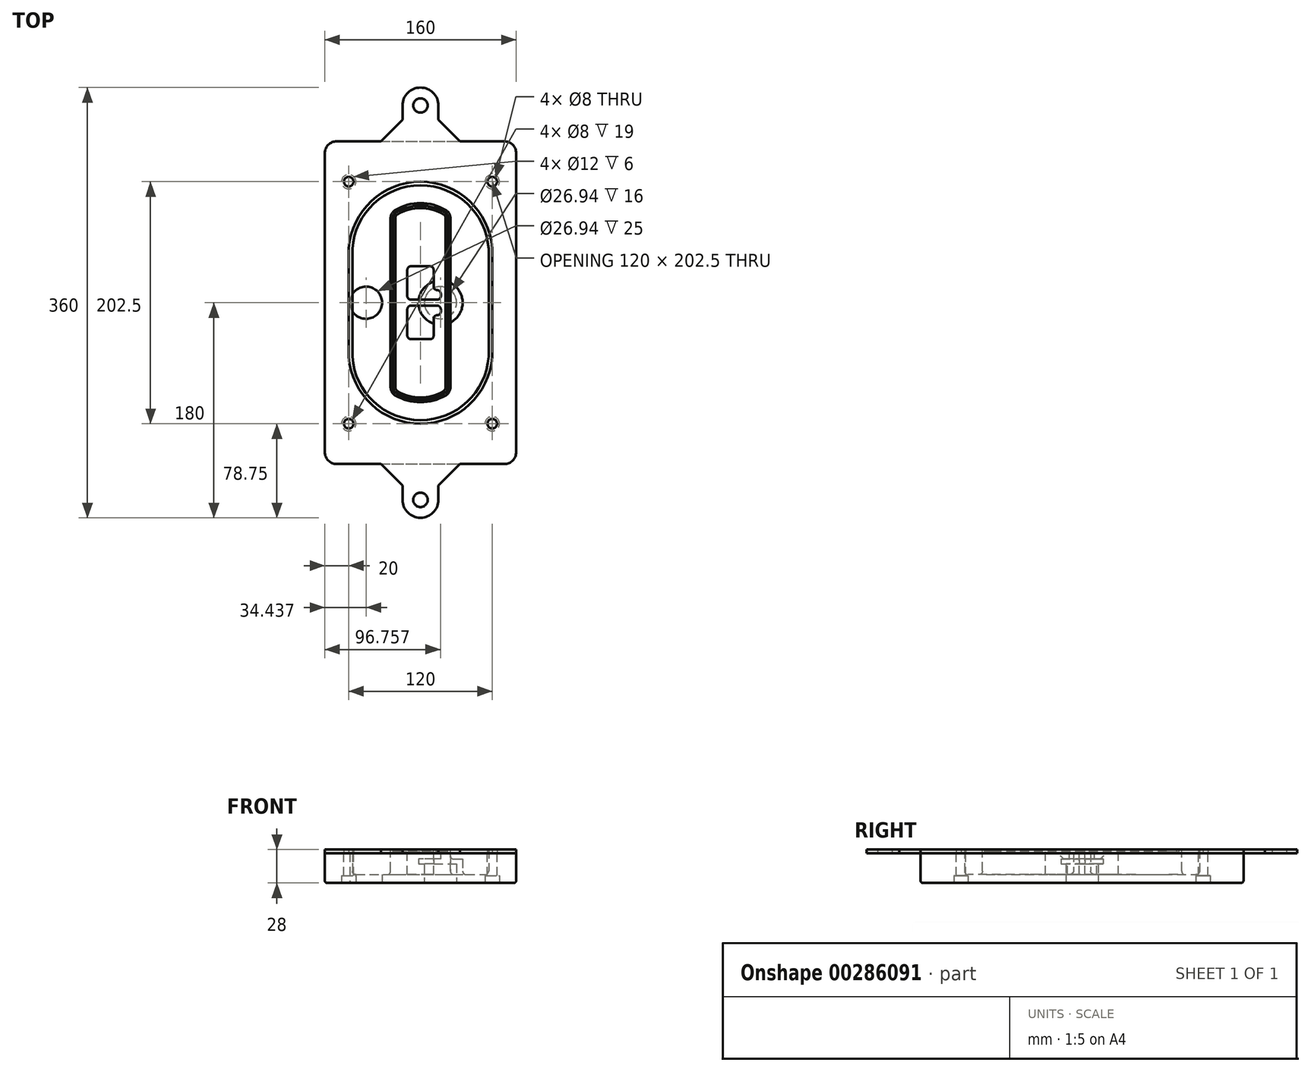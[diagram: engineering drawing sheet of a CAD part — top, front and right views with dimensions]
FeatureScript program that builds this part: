
annotation { "Feature Type Name" : "Feature", "Feature Type Description" : "" }
export const myFeature = defineFeature(function(context is Context, id is Id, definition is map)
    precondition{}
    {
        {
            var Q0;
            Q0=qCreatedBy(makeId("Top.planeOp"),FACE);
            var sketch = newSketch(context, id + "F0", { "sketchPlane" : qUnion([Q0])});
            skPoint(sketch, "E0.rect.middle", {"position": v(0, 0) * mm});
            skLineSegment(sketch, "E1.bottom", {"start": v(-70, -135) * mm, "end": v(70, -135) * mm});
            skLineSegment(sketch, "E1.top", {"start": v(-70, 135) * mm, "end": v(70, 135) * mm});
            skLineSegment(sketch, "E1.left", {"start": v(-80, -125) * mm, "end": v(-80, 125) * mm});
            skLineSegment(sketch, "E1.right", {"start": v(80, -125) * mm, "end": v(80, 125) * mm});
            skLineSegment(sketch, "E2", {"start": v(-80, 135) * mm, "end": v(80, -135) * mm, "construction": true});
            skLineSegment(sketch, "E3", {"start": v(80, 135) * mm, "end": v(-80, -135) * mm, "construction": true});
            skCircle(sketch, "E4", {"center": v(-60, 101.25) * mm, "radius": 4 * mm});
            skCircle(sketch, "E5", {"center": v(60, 101.25) * mm, "radius": 4 * mm});
            skCircle(sketch, "E6", {"center": v(60, -101.25) * mm, "radius": 4 * mm});
            skCircle(sketch, "E7", {"center": v(-60, -101.25) * mm, "radius": 4 * mm});
            skLineSegment(sketch, "E8", {"start": v(-60, 101.25) * mm, "end": v(60, 101.25) * mm, "construction": true});
            skLineSegment(sketch, "E9", {"start": v(60, 101.25) * mm, "end": v(60, -101.25) * mm, "construction": true});
            skLineSegment(sketch, "E10", {"start": v(60, -101.25) * mm, "end": v(-60, -101.25) * mm, "construction": true});
            skLineSegment(sketch, "E11", {"start": v(-60, -101.25) * mm, "end": v(-60, 101.25) * mm, "construction": true});
            skLineSegment(sketch, "E12", {"start": v(-60, 44.66) * mm, "end": v(-60, -44.66) * mm});
            skLineSegment(sketch, "E13", {"start": v(60, 44.66) * mm, "end": v(60, -44.66) * mm});
            skArc(sketch, "E14", {"start": v(59.98, 45.37) * mm, "mid": v(0, 101.25) * mm, "end": v(-59.98, 45.37) * mm});
            skArc(sketch, "E15", {"start": v(-59.98, -45.37) * mm, "mid": v(0, -101.25) * mm, "end": v(59.98, -45.37) * mm});
            skLineSegment(sketch, "E16", {"start": v(-60, 0) * mm, "end": v(60, 0) * mm, "construction": true});
            skPoint(sketch, "E17.visualSharp", {"position": v(-60, -45) * mm});
            skArc(sketch, "E17.filletArc", {"start": v(-60, -44.66) * mm, "mid": v(-60, -45.02) * mm, "end": v(-59.98, -45.37) * mm});
            skPoint(sketch, "E18.visualSharp", {"position": v(-60, 45) * mm});
            skArc(sketch, "E18.filletArc", {"start": v(-59.98, 45.37) * mm, "mid": v(-60, 45.02) * mm, "end": v(-60, 44.66) * mm});
            skPoint(sketch, "E19.visualSharp", {"position": v(60, 45) * mm});
            skArc(sketch, "E19.filletArc", {"start": v(60, 44.66) * mm, "mid": v(60, 45.02) * mm, "end": v(59.98, 45.37) * mm});
            skPoint(sketch, "E20.visualSharp", {"position": v(60, -45) * mm});
            skArc(sketch, "E20.filletArc", {"start": v(59.98, -45.37) * mm, "mid": v(60, -45.02) * mm, "end": v(60, -44.66) * mm});
            skPoint(sketch, "E21.visualSharp", {"position": v(-80, 135) * mm});
            skArc(sketch, "E21.filletArc", {"start": v(-70, 135) * mm, "mid": v(-77.07, 132.07) * mm, "end": v(-80, 125) * mm});
            skPoint(sketch, "E22.visualSharp", {"position": v(80, 135) * mm});
            skArc(sketch, "E22.filletArc", {"start": v(80, 125) * mm, "mid": v(77.07, 132.07) * mm, "end": v(70, 135) * mm});
            skPoint(sketch, "E23.visualSharp", {"position": v(80, -135) * mm});
            skArc(sketch, "E23.filletArc", {"start": v(70, -135) * mm, "mid": v(77.07, -132.07) * mm, "end": v(80, -125) * mm});
            skPoint(sketch, "E24.visualSharp", {"position": v(-80, -135) * mm});
            skArc(sketch, "E24.filletArc", {"start": v(-80, -125) * mm, "mid": v(-77.07, -132.07) * mm, "end": v(-70, -135) * mm});
            skArc(sketch, "E25.0", {"start": v(57, 44.66) * mm, "mid": v(57, 44.9) * mm, "end": v(56.98, 45.16) * mm});
            skLineSegment(sketch, "E25.1", {"start": v(57, 44.66) * mm, "end": v(57, -44.66) * mm});
            skArc(sketch, "E25.2", {"start": v(56.98, -45.16) * mm, "mid": v(57, -44.9) * mm, "end": v(57, -44.66) * mm});
            skArc(sketch, "E25.3", {"start": v(-56.98, -45.16) * mm, "mid": v(0, -98.25) * mm, "end": v(56.98, -45.16) * mm});
            skArc(sketch, "E25.4", {"start": v(-57, -44.66) * mm, "mid": v(-57, -44.9) * mm, "end": v(-56.98, -45.16) * mm});
            skArc(sketch, "E25.5", {"start": v(56.98, 45.16) * mm, "mid": v(0, 98.25) * mm, "end": v(-56.98, 45.16) * mm});
            skLineSegment(sketch, "E25.6", {"start": v(-57, 44.66) * mm, "end": v(-57, -44.66) * mm});
            skArc(sketch, "E25.7", {"start": v(-56.98, 45.16) * mm, "mid": v(-57, 44.9) * mm, "end": v(-57, 44.66) * mm});
            skArc(sketch, "E26.0", {"start": v(-63.97, 45.65) * mm, "mid": v(-64, 45.16) * mm, "end": v(-64, 44.66) * mm});
            skArc(sketch, "E26.1", {"start": v(63.97, 45.65) * mm, "mid": v(0, 105.25) * mm, "end": v(-63.97, 45.65) * mm});
            skArc(sketch, "E26.2", {"start": v(64, 44.66) * mm, "mid": v(64, 45.16) * mm, "end": v(63.97, 45.65) * mm});
            skLineSegment(sketch, "E26.3", {"start": v(64, 44.66) * mm, "end": v(64, -44.66) * mm});
            skArc(sketch, "E26.4", {"start": v(63.97, -45.65) * mm, "mid": v(64, -45.16) * mm, "end": v(64, -44.66) * mm});
            skLineSegment(sketch, "E26.5", {"start": v(-64, 44.66) * mm, "end": v(-64, -44.66) * mm});
            skArc(sketch, "E26.6", {"start": v(-63.97, -45.65) * mm, "mid": v(0, -105.25) * mm, "end": v(63.97, -45.65) * mm});
            skArc(sketch, "E26.7", {"start": v(-64, -44.66) * mm, "mid": v(-64, -45.16) * mm, "end": v(-63.97, -45.65) * mm});
            skSolve(sketch);
        }
        {
            var Q0;
            Q0=makeQuery(id+"F0.imprint","IMPRINT",FACE,{"disambiguationData":[TD([[makeQuery(id+"F0.imprint","IMPRINT",EDGE,{"derivedFrom":sQuery(id+"F0.wireOp",EDGE,"E1.bottom")}),1.0]])]});
            var Q1;
            Q1=makeQuery(id+"F0.imprint","IMPRINT",FACE,{"disambiguationData":[TD([[makeQuery(id+"F0.imprint","IMPRINT",EDGE,{"derivedFrom":sQuery(id+"F0.wireOp",EDGE,"E12")}),1.0]])]});
            var Q2;
            Q2=makeQuery(id+"F0.imprint","IMPRINT",FACE,{"disambiguationData":[TD([[makeQuery(id+"F0.imprint","IMPRINT",EDGE,{"derivedFrom":sQuery(id+"F0.wireOp",EDGE,"E25.0")}),1.0]])]});
            var Q3;
            Q3=makeQuery(id+"F0.imprint","IMPRINT",FACE,{"disambiguationData":[TD([[makeQuery(id+"F0.imprint","IMPRINT",EDGE,{"derivedFrom":sQuery(id+"F0.wireOp",EDGE,"E12")}),-1.0]])]});
            extrude(context, id + "F1", {"entities" : qUnion([Q0, Q1, Q2, Q3]), "oppositeDirection" : true, "depth" : 25 * mm});
        }
        {
            var Q0;
            Q0=makeQuery(id+"F0.imprint","IMPRINT",FACE,{"disambiguationData":[TD([[makeQuery(id+"F0.imprint","IMPRINT",EDGE,{"derivedFrom":sQuery(id+"F0.wireOp",EDGE,"E12")}),1.0]])]});
            extrude(context, id + "F2", {"entities" : qUnion([Q0]), "operationType" : NewBodyOperationType.ADD, "depth" : 3 * mm});
        }
        {
            var Q0;
            Q0=makeQuery(id+"F0.imprint","IMPRINT",FACE,{"disambiguationData":[TD([[makeQuery(id+"F0.imprint","IMPRINT",EDGE,{"derivedFrom":sQuery(id+"F0.wireOp",EDGE,"E25.0")}),1.0]])]});
            extrude(context, id + "F3", {"entities" : qUnion([Q0]), "operationType" : NewBodyOperationType.REMOVE, "oppositeDirection" : true, "depth" : 18 * mm});
        }
        {
            var Q0;
            Q0=makeQuery(id+"F2.opExtrude","CAP_FACE",FACE,{"disambiguationData":[OSD([sQuery(id+"F0.wireOp",EDGE,"E12"),sQuery(id+"F0.wireOp",EDGE,"E13"),sQuery(id+"F0.wireOp",EDGE,"E14"),sQuery(id+"F0.wireOp",EDGE,"E15"),sQuery(id+"F0.wireOp",EDGE,"E17.filletArc"),sQuery(id+"F0.wireOp",EDGE,"E18.filletArc"),sQuery(id+"F0.wireOp",EDGE,"E19.filletArc"),sQuery(id+"F0.wireOp",EDGE,"E20.filletArc"),sQuery(id+"F0.wireOp",EDGE,"E25.0"),sQuery(id+"F0.wireOp",EDGE,"E25.1"),sQuery(id+"F0.wireOp",EDGE,"E25.2"),sQuery(id+"F0.wireOp",EDGE,"E25.3"),sQuery(id+"F0.wireOp",EDGE,"E25.4"),sQuery(id+"F0.wireOp",EDGE,"E25.5"),sQuery(id+"F0.wireOp",EDGE,"E25.6"),sQuery(id+"F0.wireOp",EDGE,"E25.7")])],"isStart":false});
            var sketch = newSketch(context, id + "F4", { "sketchPlane" : qUnion([Q0])});
            skArc(sketch, "E27.0", {"start": v(-20.99, -77.65) * mm, "mid": v(0, -83.25) * mm, "end": v(20.99, -77.65) * mm});
            skArc(sketch, "E28.0", {"start": v(20.99, 77.65) * mm, "mid": v(0, 83.25) * mm, "end": v(-20.99, 77.65) * mm});
            skLineSegment(sketch, "E29", {"start": v(-25, 70.71) * mm, "end": v(-25, -70.71) * mm});
            skLineSegment(sketch, "E30", {"start": v(25, 70.71) * mm, "end": v(25, -70.71) * mm});
            skLineSegment(sketch, "E31", {"start": v(-25, 75.03) * mm, "end": v(25, 75.03) * mm, "construction": true});
            skLineSegment(sketch, "E32", {"start": v(-25, -75.03) * mm, "end": v(25, -75.03) * mm, "construction": true});
            skPoint(sketch, "E33.visualSharp", {"position": v(-25, 75.03) * mm});
            skArc(sketch, "E33.filletArc", {"start": v(-20.99, 77.65) * mm, "mid": v(-23.92, 74.72) * mm, "end": v(-25, 70.71) * mm});
            skPoint(sketch, "E34.visualSharp", {"position": v(25, 75.03) * mm});
            skArc(sketch, "E34.filletArc", {"start": v(25, 70.71) * mm, "mid": v(23.92, 74.72) * mm, "end": v(20.99, 77.65) * mm});
            skPoint(sketch, "E35.visualSharp", {"position": v(25, -75.03) * mm});
            skArc(sketch, "E35.filletArc", {"start": v(20.99, -77.65) * mm, "mid": v(23.92, -74.72) * mm, "end": v(25, -70.71) * mm});
            skPoint(sketch, "E36.visualSharp", {"position": v(-25, -75.03) * mm});
            skArc(sketch, "E36.filletArc", {"start": v(-25, -70.71) * mm, "mid": v(-23.92, -74.72) * mm, "end": v(-20.99, -77.65) * mm});
            skArc(sketch, "E37.0", {"start": v(56.98, 45.16) * mm, "mid": v(0, 98.25) * mm, "end": v(-56.98, 45.16) * mm});
            skArc(sketch, "E37.1", {"start": v(-56.98, 45.16) * mm, "mid": v(-57, 44.9) * mm, "end": v(-57, 44.66) * mm});
            skLineSegment(sketch, "E37.2", {"start": v(-57, 44.66) * mm, "end": v(-57, -44.66) * mm});
            skArc(sketch, "E37.3", {"start": v(-57, -44.66) * mm, "mid": v(-57, -44.9) * mm, "end": v(-56.98, -45.16) * mm});
            skArc(sketch, "E37.4", {"start": v(-56.98, -45.16) * mm, "mid": v(0, -98.25) * mm, "end": v(56.98, -45.16) * mm});
            skArc(sketch, "E37.5", {"start": v(56.98, -45.16) * mm, "mid": v(57, -44.9) * mm, "end": v(57, -44.66) * mm});
            skLineSegment(sketch, "E37.6", {"start": v(57, 44.66) * mm, "end": v(57, -44.66) * mm});
            skArc(sketch, "E37.7", {"start": v(57, 44.66) * mm, "mid": v(57, 44.9) * mm, "end": v(56.98, 45.16) * mm});
            skLineSegment(sketch, "E38.0", {"start": v(23, 70.71) * mm, "end": v(23, -70.71) * mm});
            skArc(sketch, "E38.1", {"start": v(19.99, -75.92) * mm, "mid": v(22.2, -73.72) * mm, "end": v(23, -70.71) * mm});
            skArc(sketch, "E38.2", {"start": v(-19.99, -75.92) * mm, "mid": v(0, -81.25) * mm, "end": v(19.99, -75.92) * mm});
            skArc(sketch, "E38.3", {"start": v(-23, -70.71) * mm, "mid": v(-22.2, -73.72) * mm, "end": v(-19.99, -75.92) * mm});
            skLineSegment(sketch, "E38.4", {"start": v(-23, 70.71) * mm, "end": v(-23, -70.71) * mm});
            skArc(sketch, "E38.5", {"start": v(23, 70.71) * mm, "mid": v(22.2, 73.72) * mm, "end": v(19.99, 75.92) * mm});
            skArc(sketch, "E38.6", {"start": v(-19.99, 75.92) * mm, "mid": v(-22.2, 73.72) * mm, "end": v(-23, 70.71) * mm});
            skArc(sketch, "E38.7", {"start": v(19.99, 75.92) * mm, "mid": v(0, 81.25) * mm, "end": v(-19.99, 75.92) * mm});
            skArc(sketch, "E39.0", {"start": v(21, 70.71) * mm, "mid": v(20.46, 72.72) * mm, "end": v(19, 74.18) * mm});
            skLineSegment(sketch, "E39.1", {"start": v(21, 70.71) * mm, "end": v(21, -70.71) * mm});
            skArc(sketch, "E39.2", {"start": v(19, -74.18) * mm, "mid": v(20.46, -72.72) * mm, "end": v(21, -70.71) * mm});
            skArc(sketch, "E39.3", {"start": v(-19, -74.18) * mm, "mid": v(0, -79.25) * mm, "end": v(19, -74.18) * mm});
            skArc(sketch, "E39.4", {"start": v(-21, -70.71) * mm, "mid": v(-20.46, -72.72) * mm, "end": v(-19, -74.18) * mm});
            skArc(sketch, "E39.5", {"start": v(19, 74.18) * mm, "mid": v(0, 79.25) * mm, "end": v(-19, 74.18) * mm});
            skLineSegment(sketch, "E39.6", {"start": v(-21, 70.71) * mm, "end": v(-21, -70.71) * mm});
            skArc(sketch, "E39.7", {"start": v(-19, 74.18) * mm, "mid": v(-20.46, 72.72) * mm, "end": v(-21, 70.71) * mm});
            skLineSegment(sketch, "E40", {"start": v(-25, 0) * mm, "end": v(25, 0) * mm, "construction": true});
            skLineSegment(sketch, "E41", {"start": v(-11, 5.5) * mm, "end": v(-11, 27.5) * mm});
            skLineSegment(sketch, "E42", {"start": v(-8, 30.5) * mm, "end": v(8, 30.5) * mm});
            skLineSegment(sketch, "E43", {"start": v(11, 27.5) * mm, "end": v(11, 13.5) * mm});
            skLineSegment(sketch, "E44", {"start": v(14, 10.5) * mm, "end": v(14, 10.5) * mm});
            skLineSegment(sketch, "E45", {"start": v(17, 7.5) * mm, "end": v(17, 5.5) * mm});
            skLineSegment(sketch, "E46", {"start": v(14, 2.5) * mm, "end": v(-8, 2.5) * mm});
            skPoint(sketch, "E47.visualSharp", {"position": v(-11, 30.5) * mm});
            skArc(sketch, "E47.filletArc", {"start": v(-8, 30.5) * mm, "mid": v(-10.12, 29.62) * mm, "end": v(-11, 27.5) * mm});
            skPoint(sketch, "E48.visualSharp", {"position": v(11, 30.5) * mm});
            skArc(sketch, "E48.filletArc", {"start": v(11, 27.5) * mm, "mid": v(10.12, 29.62) * mm, "end": v(8, 30.5) * mm});
            skPoint(sketch, "E49.visualSharp", {"position": v(11, 10.5) * mm});
            skArc(sketch, "E49.filletArc", {"start": v(11, 13.5) * mm, "mid": v(11.88, 11.38) * mm, "end": v(14, 10.5) * mm});
            skPoint(sketch, "E50.visualSharp", {"position": v(17, 10.5) * mm});
            skArc(sketch, "E50.filletArc", {"start": v(17, 7.5) * mm, "mid": v(16.12, 9.62) * mm, "end": v(14, 10.5) * mm});
            skPoint(sketch, "E51.visualSharp", {"position": v(17, 2.5) * mm});
            skArc(sketch, "E51.filletArc", {"start": v(14, 2.5) * mm, "mid": v(16.12, 3.38) * mm, "end": v(17, 5.5) * mm});
            skPoint(sketch, "E52.visualSharp", {"position": v(-11, 2.5) * mm});
            skArc(sketch, "E52.filletArc", {"start": v(-11, 5.5) * mm, "mid": v(-10.12, 3.38) * mm, "end": v(-8, 2.5) * mm});
            skLineSegment(sketch, "E53.0.MirrorCS", {"start": v(14, -2.5) * mm, "end": v(-8, -2.5) * mm});
            skArc(sketch, "E54.0.MirrorCS", {"start": v(-11, -5.5) * mm, "mid": v(-10.12, -3.38) * mm, "end": v(-8, -2.5) * mm});
            skLineSegment(sketch, "E55.0.MirrorCS", {"start": v(-11, -5.5) * mm, "end": v(-11, -27.5) * mm});
            skArc(sketch, "E56.0.MirrorCS", {"start": v(-8, -30.5) * mm, "mid": v(-10.12, -29.62) * mm, "end": v(-11, -27.5) * mm});
            skLineSegment(sketch, "E57.0.MirrorCS", {"start": v(-8, -30.5) * mm, "end": v(8, -30.5) * mm});
            skArc(sketch, "E58.0.MirrorCS", {"start": v(11, -27.5) * mm, "mid": v(10.12, -29.62) * mm, "end": v(8, -30.5) * mm});
            skLineSegment(sketch, "E59.0.MirrorCS", {"start": v(11, -27.5) * mm, "end": v(11, -13.5) * mm});
            skArc(sketch, "E60.0.MirrorCS", {"start": v(11, -13.5) * mm, "mid": v(11.88, -11.38) * mm, "end": v(14, -10.5) * mm});
            skArc(sketch, "E61.0.MirrorCS", {"start": v(17, -7.5) * mm, "mid": v(16.12, -9.62) * mm, "end": v(14, -10.5) * mm});
            skLineSegment(sketch, "E62.0.MirrorCS", {"start": v(17, -7.5) * mm, "end": v(17, -5.5) * mm});
            skArc(sketch, "E63.0.MirrorCS", {"start": v(14, -2.5) * mm, "mid": v(16.12, -3.38) * mm, "end": v(17, -5.5) * mm});
            skSolve(sketch);
        }
        {
            var Q0;
            Q0=makeQuery(id+"F4.imprint","IMPRINT",FACE,{"disambiguationData":[TD([[makeQuery(id+"F4.imprint","IMPRINT",EDGE,{"derivedFrom":sQuery(id+"F4.wireOp",EDGE,"E27.0")}),1.0]])]});
            var Q1;
            Q1=makeQuery(id+"F4.imprint","IMPRINT",FACE,{"disambiguationData":[TD([[makeQuery(id+"F4.imprint","IMPRINT",EDGE,{"derivedFrom":sQuery(id+"F4.wireOp",EDGE,"E38.0")}),-1.0]])]});
            var Q2;
            Q2=makeQuery(id+"F4.imprint","IMPRINT",FACE,{"disambiguationData":[TD([[makeQuery(id+"F4.imprint","IMPRINT",EDGE,{"derivedFrom":sQuery(id+"F4.wireOp",EDGE,"E39.0")}),1.0]])]});
            extrude(context, id + "F5", {"entities" : qUnion([Q0, Q1, Q2]), "operationType" : NewBodyOperationType.ADD, "endBound" : BoundingType.UP_TO_NEXT, "oppositeDirection" : true, "depth" : 25 * mm});
        }
        {
            var Q0;
            Q0=makeQuery(id+"F4.imprint","IMPRINT",FACE,{"disambiguationData":[TD([[makeQuery(id+"F4.imprint","IMPRINT",EDGE,{"derivedFrom":sQuery(id+"F4.wireOp",EDGE,"E38.0")}),-1.0]])]});
            extrude(context, id + "F6", {"entities" : qUnion([Q0]), "operationType" : NewBodyOperationType.REMOVE, "oppositeDirection" : true, "depth" : 2 * mm});
        }
        {
            var Q0;
            Q0=makeQuery(id+"F1.opExtrude","CAP_FACE",FACE,{"disambiguationData":[OSD([sQuery(id+"F0.wireOp",EDGE,"E1.bottom"),sQuery(id+"F0.wireOp",EDGE,"E1.top"),sQuery(id+"F0.wireOp",EDGE,"E1.left"),sQuery(id+"F0.wireOp",EDGE,"E1.right"),sQuery(id+"F0.wireOp",EDGE,"E4"),sQuery(id+"F0.wireOp",EDGE,"E5"),sQuery(id+"F0.wireOp",EDGE,"E6"),sQuery(id+"F0.wireOp",EDGE,"E7"),sQuery(id+"F0.wireOp",EDGE,"E21.filletArc"),sQuery(id+"F0.wireOp",EDGE,"E22.filletArc"),sQuery(id+"F0.wireOp",EDGE,"E23.filletArc"),sQuery(id+"F0.wireOp",EDGE,"E24.filletArc")])],"isStart":false});
            var sketch = newSketch(context, id + "F7", { "sketchPlane" : qUnion([Q0])});
            skCircle(sketch, "E64", {"center": v(16.76, 0) * mm, "radius": 13.47 * mm});
            skCircle(sketch, "E65", {"center": v(-45.56, 0) * mm, "radius": 13.47 * mm});
            skLineSegment(sketch, "E66", {"start": v(80, 0) * mm, "end": v(-80, 0) * mm});
            skCircle(sketch, "E67", {"center": v(16.76, 0) * mm, "radius": 18.47 * mm});
            skCircle(sketch, "E68", {"center": v(60, -101.25) * mm, "radius": 6 * mm});
            skCircle(sketch, "E69", {"center": v(-60, -101.25) * mm, "radius": 6 * mm});
            skCircle(sketch, "E70", {"center": v(-60, 101.25) * mm, "radius": 6 * mm});
            skCircle(sketch, "E71", {"center": v(60, 101.25) * mm, "radius": 6 * mm});
            skSolve(sketch);
        }
        {
            var Q0;
            {var subQ1=sQuery(id+"F7.wireOp",EDGE,"E66");var subQ4=sQuery(id+"F7.wireOp",EDGE,"E64");var subQ6=makeQuery(id+"F7.imprint","INTERSECT",VERTEX,{"disambiguationData":[OD(0.0)],"derivedFrom":[subQ4,subQ1]});Q0=makeQuery(id+"F7.imprint","IMPRINT",FACE,{"disambiguationData":[TD([[makeQuery(id+"F7.imprint","IMPRINT",EDGE,{"disambiguationData":[TD([[subQ6,-1.0]])],"derivedFrom":subQ4}),-1.0]])]});}
            var Q1;
            {var subQ0=sQuery(id+"F7.wireOp",EDGE,"E66");var subQ1=sQuery(id+"F7.wireOp",EDGE,"E64");var subQ3=makeQuery(id+"F7.imprint","INTERSECT",VERTEX,{"disambiguationData":[OD(0.0)],"derivedFrom":[subQ1,subQ0]});Q1=makeQuery(id+"F7.imprint","IMPRINT",FACE,{"disambiguationData":[TD([[makeQuery(id+"F7.imprint","IMPRINT",EDGE,{"disambiguationData":[TD([[subQ3,-1.0]])],"derivedFrom":subQ1}),1.0]])]});}
            var Q2;
            {var subQ0=sQuery(id+"F7.wireOp",EDGE,"E66");var subQ1=sQuery(id+"F7.wireOp",EDGE,"E64");var subQ3=makeQuery(id+"F7.imprint","INTERSECT",VERTEX,{"disambiguationData":[OD(0.0)],"derivedFrom":[subQ1,subQ0]});Q2=makeQuery(id+"F7.imprint","IMPRINT",FACE,{"disambiguationData":[TD([[makeQuery(id+"F7.imprint","IMPRINT",EDGE,{"disambiguationData":[TD([[subQ3,1.0]])],"derivedFrom":subQ1}),1.0]])]});}
            var Q3;
            {var subQ1=sQuery(id+"F7.wireOp",EDGE,"E66");var subQ4=sQuery(id+"F7.wireOp",EDGE,"E64");var subQ6=makeQuery(id+"F7.imprint","INTERSECT",VERTEX,{"disambiguationData":[OD(0.0)],"derivedFrom":[subQ4,subQ1]});Q3=makeQuery(id+"F7.imprint","IMPRINT",FACE,{"disambiguationData":[TD([[makeQuery(id+"F7.imprint","IMPRINT",EDGE,{"disambiguationData":[TD([[subQ6,1.0]])],"derivedFrom":subQ4}),-1.0]])]});}
            extrude(context, id + "F8", {"entities" : qUnion([Q0, Q1, Q2, Q3]), "operationType" : NewBodyOperationType.ADD, "oppositeDirection" : true, "depth" : 20 * mm});
        }
        {
            var Q0;
            {var subQ0=sQuery(id+"F7.wireOp",EDGE,"E66");var subQ1=sQuery(id+"F7.wireOp",EDGE,"E64");var subQ3=makeQuery(id+"F7.imprint","INTERSECT",VERTEX,{"disambiguationData":[OD(0.0)],"derivedFrom":[subQ1,subQ0]});Q0=makeQuery(id+"F7.imprint","IMPRINT",FACE,{"disambiguationData":[TD([[makeQuery(id+"F7.imprint","IMPRINT",EDGE,{"disambiguationData":[TD([[subQ3,-1.0]])],"derivedFrom":subQ1}),1.0]])]});}
            var Q1;
            {var subQ0=sQuery(id+"F7.wireOp",EDGE,"E66");var subQ1=sQuery(id+"F7.wireOp",EDGE,"E64");var subQ3=makeQuery(id+"F7.imprint","INTERSECT",VERTEX,{"disambiguationData":[OD(0.0)],"derivedFrom":[subQ1,subQ0]});Q1=makeQuery(id+"F7.imprint","IMPRINT",FACE,{"disambiguationData":[TD([[makeQuery(id+"F7.imprint","IMPRINT",EDGE,{"disambiguationData":[TD([[subQ3,1.0]])],"derivedFrom":subQ1}),1.0]])]});}
            extrude(context, id + "F9", {"entities" : qUnion([Q0, Q1]), "operationType" : NewBodyOperationType.REMOVE, "oppositeDirection" : true, "depth" : 16 * mm});
        }
        {
            var Q0;
            {var subQ0=sQuery(id+"F7.wireOp",EDGE,"E66");var subQ1=sQuery(id+"F7.wireOp",EDGE,"E65");var subQ3=makeQuery(id+"F7.imprint","INTERSECT",VERTEX,{"disambiguationData":[OD(0.0)],"derivedFrom":[subQ1,subQ0]});Q0=makeQuery(id+"F7.imprint","IMPRINT",FACE,{"disambiguationData":[TD([[makeQuery(id+"F7.imprint","IMPRINT",EDGE,{"disambiguationData":[TD([[subQ3,-1.0]])],"derivedFrom":subQ1}),1.0]])]});}
            var Q1;
            {var subQ0=sQuery(id+"F7.wireOp",EDGE,"E66");var subQ1=sQuery(id+"F7.wireOp",EDGE,"E65");var subQ3=makeQuery(id+"F7.imprint","INTERSECT",VERTEX,{"disambiguationData":[OD(0.0)],"derivedFrom":[subQ1,subQ0]});Q1=makeQuery(id+"F7.imprint","IMPRINT",FACE,{"disambiguationData":[TD([[makeQuery(id+"F7.imprint","IMPRINT",EDGE,{"disambiguationData":[TD([[subQ3,1.0]])],"derivedFrom":subQ1}),1.0]])]});}
            extrude(context, id + "F10", {"entities" : qUnion([Q0, Q1]), "operationType" : NewBodyOperationType.REMOVE, "oppositeDirection" : true, "depth" : 25 * mm});
        }
        {
            var Q0;
            Q0=makeQuery(id+"F7.imprint","IMPRINT",FACE,{"disambiguationData":[TD([[makeQuery(id+"F7.imprint","IMPRINT",EDGE,{"derivedFrom":sQuery(id+"F7.wireOp",EDGE,"E68")}),1.0]])]});
            var Q1;
            Q1=makeQuery(id+"F7.imprint","IMPRINT",FACE,{"disambiguationData":[TD([[makeQuery(id+"F7.imprint","IMPRINT",EDGE,{"derivedFrom":makeQuery(id+"F1.opExtrude","CAP_EDGE",EDGE,{"disambiguationData":[OSD([sQuery(id+"F0.wireOp",EDGE,"E5")])],"isStart":false})}),-1.0]])]});
            var Q2;
            Q2=makeQuery(id+"F7.imprint","IMPRINT",FACE,{"disambiguationData":[TD([[makeQuery(id+"F7.imprint","IMPRINT",EDGE,{"derivedFrom":sQuery(id+"F7.wireOp",EDGE,"E69")}),1.0]])]});
            var Q3;
            Q3=makeQuery(id+"F7.imprint","IMPRINT",FACE,{"disambiguationData":[TD([[makeQuery(id+"F7.imprint","IMPRINT",EDGE,{"derivedFrom":makeQuery(id+"F1.opExtrude","CAP_EDGE",EDGE,{"disambiguationData":[OSD([sQuery(id+"F0.wireOp",EDGE,"E4")])],"isStart":false})}),-1.0]])]});
            var Q4;
            Q4=makeQuery(id+"F7.imprint","IMPRINT",FACE,{"disambiguationData":[TD([[makeQuery(id+"F7.imprint","IMPRINT",EDGE,{"derivedFrom":sQuery(id+"F7.wireOp",EDGE,"E70")}),1.0]])]});
            var Q5;
            Q5=makeQuery(id+"F7.imprint","IMPRINT",FACE,{"disambiguationData":[TD([[makeQuery(id+"F7.imprint","IMPRINT",EDGE,{"derivedFrom":makeQuery(id+"F1.opExtrude","CAP_EDGE",EDGE,{"disambiguationData":[OSD([sQuery(id+"F0.wireOp",EDGE,"E7")])],"isStart":false})}),-1.0]])]});
            var Q6;
            Q6=makeQuery(id+"F7.imprint","IMPRINT",FACE,{"disambiguationData":[TD([[makeQuery(id+"F7.imprint","IMPRINT",EDGE,{"derivedFrom":sQuery(id+"F7.wireOp",EDGE,"E71")}),1.0]])]});
            var Q7;
            Q7=makeQuery(id+"F7.imprint","IMPRINT",FACE,{"disambiguationData":[TD([[makeQuery(id+"F7.imprint","IMPRINT",EDGE,{"derivedFrom":makeQuery(id+"F1.opExtrude","CAP_EDGE",EDGE,{"disambiguationData":[OSD([sQuery(id+"F0.wireOp",EDGE,"E6")])],"isStart":false})}),-1.0]])]});
            extrude(context, id + "F11", {"entities" : qUnion([Q0, Q1, Q2, Q3, Q4, Q5, Q6, Q7]), "operationType" : NewBodyOperationType.REMOVE, "oppositeDirection" : true, "depth" : 6 * mm});
        }
        {
            var Q0;
            Q0=makeQuery(id+"F9.boolean.opBoolean","COPY",FACE,{"derivedFrom":makeQuery(id+"F9.opExtrude","CAP_FACE",FACE,{"disambiguationData":[OSD([sQuery(id+"F7.wireOp",EDGE,"E64")])],"isStart":false})});
            var sketch = newSketch(context, id + "F12", { "sketchPlane" : qUnion([Q0])});
            skArc(sketch, "E72.0", {"start": v(11, 17.55) * mm, "mid": v(2.57, 11.82) * mm, "end": v(-1.54, 2.5) * mm});
            skArc(sketch, "E72.1", {"start": v(-1.54, -2.5) * mm, "mid": v(2.57, -11.82) * mm, "end": v(11, -17.55) * mm});
            skLineSegment(sketch, "E73", {"start": v(-1.54, -2.5) * mm, "end": v(14, -2.5) * mm});
            skLineSegment(sketch, "E74.0", {"start": v(14, 2.5) * mm, "end": v(-1.54, 2.5) * mm});
            skArc(sketch, "E74.1", {"start": v(14, 2.5) * mm, "mid": v(16.12, 3.38) * mm, "end": v(17, 5.5) * mm});
            skLineSegment(sketch, "E74.2", {"start": v(17, 7.5) * mm, "end": v(17, 5.5) * mm});
            skArc(sketch, "E74.3", {"start": v(17, 7.5) * mm, "mid": v(16.12, 9.62) * mm, "end": v(14, 10.5) * mm});
            skArc(sketch, "E74.4", {"start": v(11, 13.5) * mm, "mid": v(11.88, 11.38) * mm, "end": v(14, 10.5) * mm});
            skLineSegment(sketch, "E74.5", {"start": v(11, 17.55) * mm, "end": v(11, 13.5) * mm});
            skLineSegment(sketch, "E74.7", {"start": v(14, -2.5) * mm, "end": v(-1.54, -2.5) * mm});
            skArc(sketch, "E74.8", {"start": v(14, -2.5) * mm, "mid": v(16.12, -3.38) * mm, "end": v(17, -5.5) * mm});
            skLineSegment(sketch, "E74.9", {"start": v(17, -7.5) * mm, "end": v(17, -5.5) * mm});
            skArc(sketch, "E74.10", {"start": v(17, -7.5) * mm, "mid": v(16.12, -9.62) * mm, "end": v(14, -10.5) * mm});
            skArc(sketch, "E74.11", {"start": v(11, -13.5) * mm, "mid": v(11.88, -11.38) * mm, "end": v(14, -10.5) * mm});
            skLineSegment(sketch, "E74.12", {"start": v(11, -17.55) * mm, "end": v(11, -13.5) * mm});
            skPoint(sketch, "E75.orphan", {"position": v(11, -27.5) * mm});
            skPoint(sketch, "E76.orphan", {"position": v(-8, -2.5) * mm});
            skPoint(sketch, "E77.orphan", {"position": v(-8, 2.5) * mm});
            skPoint(sketch, "E78.orphan", {"position": v(11, 27.5) * mm});
            skSolve(sketch);
        }
        {
            var Q0;
            {var subQ7=sQuery(id+"F12.wireOp",EDGE,"E72.0");var subQ14=sQuery(id+"F12.wireOp",EDGE,"E72.1");var subQ16=sQuery(id+"F12.wireOp",EDGE,"E74.1");var subQ18=sQuery(id+"F12.wireOp",EDGE,"E74.8");Q0=qUnion([makeQuery(id+"F12.imprint","IMPRINT",FACE,{"disambiguationData":[TD([[makeQuery(id+"F12.imprint","IMPRINT",EDGE,{"derivedFrom":subQ7}),1.0]])]}),makeQuery(id+"F12.imprint","IMPRINT",FACE,{"disambiguationData":[TD([[makeQuery(id+"F12.imprint","IMPRINT",EDGE,{"derivedFrom":subQ14}),1.0]])]}),makeQuery(id+"F12.imprint","IMPRINT",FACE,{"disambiguationData":[TD([[makeQuery(id+"F12.imprint","IMPRINT",EDGE,{"derivedFrom":subQ16}),1.0]])]}),makeQuery(id+"F12.imprint","IMPRINT",FACE,{"disambiguationData":[TD([[makeQuery(id+"F12.imprint","IMPRINT",EDGE,{"derivedFrom":subQ18}),-1.0]])]})]);}
            var Q1;
            Q1=makeQuery(id+"F5.boolean.opBoolean","SPLIT",FACE,{"disambiguationData":[TD([makeQuery(id+"F5.opExtrude","SWEPT_FACE",FACE,{"disambiguationData":[OSD([sQuery(id+"F4.wireOp",EDGE,"E41")])]})])],"derivedFrom":makeQuery(id+"F3.boolean.opBoolean","COPY",FACE,{"derivedFrom":makeQuery(id+"F3.opExtrude","CAP_FACE",FACE,{"disambiguationData":[OSD([sQuery(id+"F0.wireOp",EDGE,"E25.0"),sQuery(id+"F0.wireOp",EDGE,"E25.1"),sQuery(id+"F0.wireOp",EDGE,"E25.2"),sQuery(id+"F0.wireOp",EDGE,"E25.3"),sQuery(id+"F0.wireOp",EDGE,"E25.4"),sQuery(id+"F0.wireOp",EDGE,"E25.5"),sQuery(id+"F0.wireOp",EDGE,"E25.6"),sQuery(id+"F0.wireOp",EDGE,"E25.7")])],"isStart":false})})});
            extrude(context, id + "F13", {"entities" : qUnion([Q0]), "operationType" : NewBodyOperationType.REMOVE, "endBound" : BoundingType.UP_TO_SURFACE, "endBoundEntityFace" : qUnion([Q1]), "depth" : 25 * mm});
        }
        {
            var Q0;
            Q0=makeQuery(id+"F3.boolean.opBoolean","COPY",EDGE,{"derivedFrom":makeQuery(id+"F3.opExtrude","CAP_EDGE",EDGE,{"disambiguationData":[OSD([sQuery(id+"F0.wireOp",EDGE,"E25.6")])],"isStart":false})});
            var Q1;
            Q1=makeQuery(id+"F8.boolean.opBoolean","INTERSECT",EDGE,{"derivedFrom":[makeQuery(id+"F5.opExtrude","SWEPT_FACE",FACE,{"disambiguationData":[OSD([sQuery(id+"F4.wireOp",EDGE,"E30")])]}),makeQuery(id+"F8.opExtrude","CAP_FACE",FACE,{"disambiguationData":[OSD([sQuery(id+"F7.wireOp",EDGE,"E67")])],"isStart":false})]});
            var Q2;
            Q2=makeQuery(id+"F8.boolean.opBoolean","INTERSECT",EDGE,{"disambiguationData":[OD(1.0)],"derivedFrom":[makeQuery(id+"F5.opExtrude","SWEPT_FACE",FACE,{"disambiguationData":[OSD([sQuery(id+"F4.wireOp",EDGE,"E30")])]}),makeQuery(id+"F8.opExtrude","SWEPT_FACE",FACE,{"disambiguationData":[OSD([sQuery(id+"F7.wireOp",EDGE,"E67")])]})]});
            var Q3;
            {var subQ0=sQuery(id+"F4.wireOp",EDGE,"E30");Q3=makeQuery(id+"F8.boolean.opBoolean","SPLIT",EDGE,{"disambiguationData":[TD([makeQuery(id+"F5.opExtrude","SWEPT_FACE",FACE,{"disambiguationData":[OSD([sQuery(id+"F4.wireOp",EDGE,"E35.filletArc")])]})])],"derivedFrom":makeQuery(id+"F5.opExtrude","CAP_EDGE",EDGE,{"disambiguationData":[OSD([subQ0])],"isStart":false})});}
            var Q4;
            {var subQ0=sQuery(id+"F0.wireOp",EDGE,"E25.7");var subQ1=sQuery(id+"F0.wireOp",EDGE,"E25.1");var subQ2=sQuery(id+"F0.wireOp",EDGE,"E25.6");var subQ3=sQuery(id+"F0.wireOp",EDGE,"E25.5");var subQ4=sQuery(id+"F0.wireOp",EDGE,"E25.4");var subQ5=sQuery(id+"F0.wireOp",EDGE,"E25.0");var subQ6=sQuery(id+"F0.wireOp",EDGE,"E25.2");var subQ7=sQuery(id+"F0.wireOp",EDGE,"E25.3");Q4=makeQuery(id+"F8.boolean.opBoolean","INTERSECT",EDGE,{"derivedFrom":[makeQuery(id+"F5.boolean.opBoolean","SPLIT",FACE,{"disambiguationData":[TD([makeQuery(id+"F2.opExtrude","SWEPT_FACE",FACE,{"disambiguationData":[OSD([subQ5])]})])],"derivedFrom":makeQuery(id+"F3.boolean.opBoolean","COPY",FACE,{"derivedFrom":makeQuery(id+"F3.opExtrude","CAP_FACE",FACE,{"disambiguationData":[OSD([subQ5,subQ1,subQ6,subQ7,subQ4,subQ3,subQ2,subQ0])],"isStart":false})})}),makeQuery(id+"F8.opExtrude","SWEPT_FACE",FACE,{"disambiguationData":[OSD([sQuery(id+"F7.wireOp",EDGE,"E67")])]})]});}
            var Q5;
            Q5=makeQuery(id+"F8.boolean.opBoolean","INTERSECT",EDGE,{"disambiguationData":[OD(0.0)],"derivedFrom":[makeQuery(id+"F5.opExtrude","SWEPT_FACE",FACE,{"disambiguationData":[OSD([sQuery(id+"F4.wireOp",EDGE,"E30")])]}),makeQuery(id+"F8.opExtrude","SWEPT_FACE",FACE,{"disambiguationData":[OSD([sQuery(id+"F7.wireOp",EDGE,"E67")])]})]});
            fillet(context, id + "F14", {"entities" : qUnion([Q0, Q1, Q2, Q3, Q4, Q5]), "radius" : 3 * mm, "tangentPropagation" : true, "allowEdgeOverflow" : false});
        }
        {
            var Q0;
            Q0=makeQuery(id+"F1.opExtrude","CAP_EDGE",EDGE,{"disambiguationData":[OSD([sQuery(id+"F0.wireOp",EDGE,"E1.bottom")])],"isStart":false});
            fillet(context, id + "F15", {"entities" : qUnion([Q0]), "radius" : 2 * mm, "tangentPropagation" : true, "allowEdgeOverflow" : false});
        }
        {
            var Q0;
            {var subQ0=sQuery(id+"F0.wireOp",EDGE,"E21.filletArc");var subQ1=sQuery(id+"F0.wireOp",EDGE,"E7");var subQ2=sQuery(id+"F0.wireOp",EDGE,"E6");var subQ3=sQuery(id+"F0.wireOp",EDGE,"E5");var subQ4=sQuery(id+"F0.wireOp",EDGE,"E4");var subQ5=sQuery(id+"F0.wireOp",EDGE,"E22.filletArc");var subQ6=sQuery(id+"F0.wireOp",EDGE,"E1.bottom");var subQ7=sQuery(id+"F0.wireOp",EDGE,"E1.right");var subQ8=sQuery(id+"F0.wireOp",EDGE,"E1.top");var subQ9=sQuery(id+"F0.wireOp",EDGE,"E1.left");var subQ10=sQuery(id+"F0.wireOp",EDGE,"E23.filletArc");var subQ11=sQuery(id+"F0.wireOp",EDGE,"E24.filletArc");Q0=makeQuery(id+"F2.boolean.opBoolean","SPLIT",FACE,{"disambiguationData":[TD([makeQuery(id+"F1.opExtrude","SWEPT_FACE",FACE,{"disambiguationData":[OSD([subQ6])]})])],"derivedFrom":makeQuery(id+"F1.opExtrude","CAP_FACE",FACE,{"disambiguationData":[OSD([subQ6,subQ8,subQ9,subQ7,subQ4,subQ3,subQ2,subQ1,subQ0,subQ5,subQ10,subQ11])],"isStart":true})});}
            var sketch = newSketch(context, id + "F16", { "sketchPlane" : qUnion([Q0])});
            skLineSegment(sketch, "E79.0", {"start": v(14, 2.5) * mm, "end": v(-8, 2.5) * mm});
            skPoint(sketch, "E80.0", {"position": v(0, 0) * mm});
            skPoint(sketch, "E81.0", {"position": v(0, 135) * mm});
            skLineSegment(sketch, "E82", {"start": v(0, 135) * mm, "end": v(0, 165) * mm, "construction": true});
            skCircle(sketch, "E83", {"center": v(0, 165) * mm, "radius": 6 * mm});
            skArc(sketch, "E84", {"start": v(-15, 165) * mm, "mid": v(0, 180) * mm, "end": v(15, 165) * mm});
            skLineSegment(sketch, "E85", {"start": v(-15, 165) * mm, "end": v(-15, 153) * mm});
            skLineSegment(sketch, "E86", {"start": v(15, 165) * mm, "end": v(15, 153) * mm});
            skLineSegment(sketch, "E87", {"start": v(15, 153) * mm, "end": v(33, 135) * mm});
            skLineSegment(sketch, "E88", {"start": v(-15, 153) * mm, "end": v(-33, 135) * mm});
            skLineSegment(sketch, "E89.0.0", {"start": v(70, 135) * mm, "end": v(-70, 135) * mm});
            skArc(sketch, "E89.0.1", {"start": v(-70, 135) * mm, "mid": v(-77.07, 132.07) * mm, "end": v(-80, 125) * mm});
            skLineSegment(sketch, "E89.0.2", {"start": v(-80, 125) * mm, "end": v(-80, -125) * mm});
            skArc(sketch, "E89.0.3", {"start": v(-80, -125) * mm, "mid": v(-77.07, -132.07) * mm, "end": v(-70, -135) * mm});
            skLineSegment(sketch, "E89.0.4", {"start": v(-70, -135) * mm, "end": v(70, -135) * mm});
            skArc(sketch, "E89.0.5", {"start": v(70, -135) * mm, "mid": v(77.07, -132.07) * mm, "end": v(80, -125) * mm});
            skLineSegment(sketch, "E89.0.6", {"start": v(80, -125) * mm, "end": v(80, 125) * mm});
            skArc(sketch, "E89.0.7", {"start": v(80, 125) * mm, "mid": v(77.07, 132.07) * mm, "end": v(70, 135) * mm});
            skLineSegment(sketch, "E90", {"start": v(-80, 0) * mm, "end": v(80, 0) * mm, "construction": true});
            skLineSegment(sketch, "E91.MirrorCS", {"start": v(-15, -153) * mm, "end": v(-33, -135) * mm});
            skLineSegment(sketch, "E92.MirrorCS", {"start": v(-15, -165) * mm, "end": v(-15, -153) * mm});
            skArc(sketch, "E93.MirrorCS", {"start": v(-15, -165) * mm, "mid": v(0, -180) * mm, "end": v(15, -165) * mm});
            skCircle(sketch, "E94.MirrorC", {"center": v(0, -165) * mm, "radius": 6 * mm});
            skLineSegment(sketch, "E95.MirrorCS", {"start": v(15, -165) * mm, "end": v(15, -153) * mm});
            skLineSegment(sketch, "E96.MirrorCS", {"start": v(15, -153) * mm, "end": v(33, -135) * mm});
            skSolve(sketch);
        }
        {
            var Q0;
            {var subQ1=sQuery(id+"F16.wireOp",EDGE,"E89.0.1");Q0=makeQuery(id+"F16.imprint","IMPRINT",FACE,{"disambiguationData":[TD([[makeQuery(id+"F16.imprint","IMPRINT",EDGE,{"derivedFrom":subQ1}),1.0]])]});}
            var Q1;
            Q1=makeQuery(id+"F16.imprint","IMPRINT",FACE,{"disambiguationData":[TD([[makeQuery(id+"F16.imprint","IMPRINT",EDGE,{"derivedFrom":sQuery(id+"F16.wireOp",EDGE,"E83")}),-1.0]])]});
            var Q2;
            {var subQ0=sQuery(id+"F16.wireOp",EDGE,"E91.MirrorCS");Q2=makeQuery(id+"F16.imprint","IMPRINT",FACE,{"disambiguationData":[TD([[makeQuery(id+"F16.imprint","IMPRINT",EDGE,{"derivedFrom":subQ0}),-1.0]])]});}
            var Q3;
            Q3=makeQuery(id+"F2.opExtrude","CAP_FACE",FACE,{"disambiguationData":[OSD([sQuery(id+"F0.wireOp",EDGE,"E12"),sQuery(id+"F0.wireOp",EDGE,"E13"),sQuery(id+"F0.wireOp",EDGE,"E14"),sQuery(id+"F0.wireOp",EDGE,"E15"),sQuery(id+"F0.wireOp",EDGE,"E17.filletArc"),sQuery(id+"F0.wireOp",EDGE,"E18.filletArc"),sQuery(id+"F0.wireOp",EDGE,"E19.filletArc"),sQuery(id+"F0.wireOp",EDGE,"E20.filletArc"),sQuery(id+"F0.wireOp",EDGE,"E25.0"),sQuery(id+"F0.wireOp",EDGE,"E25.1"),sQuery(id+"F0.wireOp",EDGE,"E25.2"),sQuery(id+"F0.wireOp",EDGE,"E25.3"),sQuery(id+"F0.wireOp",EDGE,"E25.4"),sQuery(id+"F0.wireOp",EDGE,"E25.5"),sQuery(id+"F0.wireOp",EDGE,"E25.6"),sQuery(id+"F0.wireOp",EDGE,"E25.7")])],"isStart":false});
            extrude(context, id + "F17", {"entities" : qUnion([Q0, Q1, Q2]), "endBound" : BoundingType.UP_TO_SURFACE, "endBoundEntityFace" : qUnion([Q3]), "depth" : 25 * mm});
        }
    });
